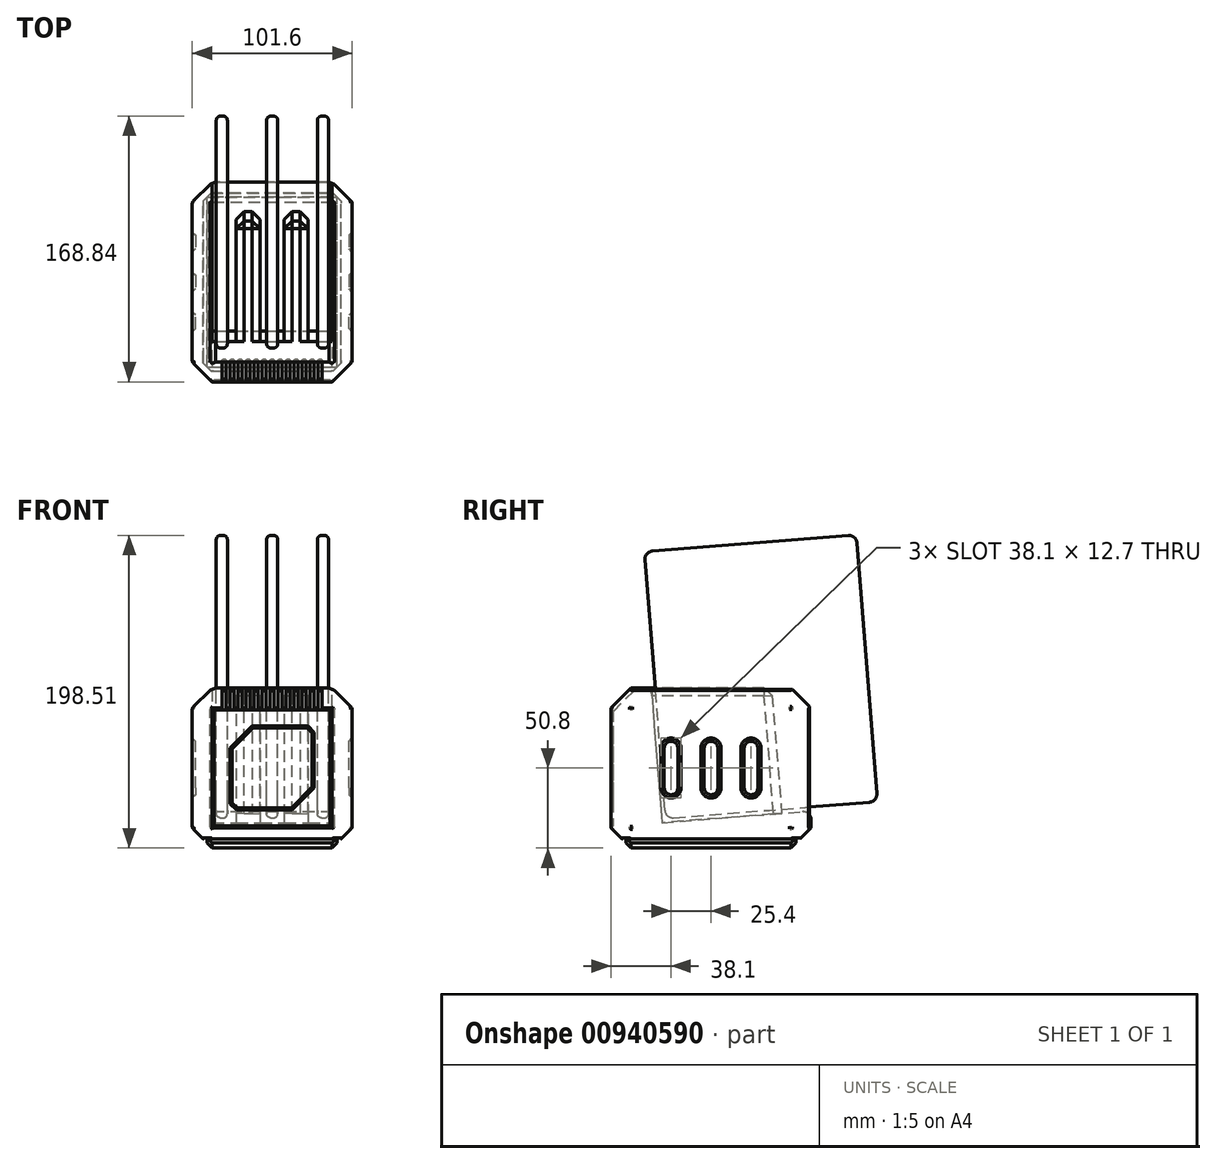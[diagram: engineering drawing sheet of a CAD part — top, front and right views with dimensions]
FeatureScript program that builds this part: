
annotation { "Feature Type Name" : "Feature", "Feature Type Description" : "" }
export const myFeature = defineFeature(function(context is Context, id is Id, definition is map)
    precondition{}
    {
        {
            var Q0;
            Q0=qCreatedBy(makeId("Front.planeOp"),FACE);
            var sketch = newSketch(context, id + "F0", { "sketchPlane" : qUnion([Q0])});
            skLineSegment(sketch, "E0.bottom", {"start": v(-50.8, 50.8) * mm, "end": v(50.8, 50.8) * mm});
            skLineSegment(sketch, "E0.top", {"start": v(-50.8, -50.8) * mm, "end": v(50.8, -50.8) * mm});
            skLineSegment(sketch, "E0.left", {"start": v(-50.8, 50.8) * mm, "end": v(-50.8, -50.8) * mm});
            skLineSegment(sketch, "E0.right", {"start": v(50.8, 50.8) * mm, "end": v(50.8, -50.8) * mm});
            skSolve(sketch);
        }
        {
            var Q0;
            Q0=makeQuery(id+"F0.imprint","IMPRINT",FACE,{"disambiguationData":[TD([[makeQuery(id+"F0.imprint","IMPRINT",EDGE,{"derivedFrom":sQuery(id+"F0.wireOp",EDGE,"E0.bottom")}),-1.0]])]});
            extrude(context, id + "F1", {"entities" : qUnion([Q0]), "endBound" : BoundingType.SYMMETRIC, "depth" : 127 * mm, "offsetDistance" : 25.4 * mm});
        }
        {
            var Q0;
            Q0=makeQuery(id+"F1.opExtrude","SWEPT_FACE",FACE,{"disambiguationData":[OSD([sQuery(id+"F0.wireOp",EDGE,"E0.bottom")])]});
            var Q1;
            Q1=makeQuery(id+"F1.opExtrude","SWEPT_FACE",FACE,{"disambiguationData":[OSD([sQuery(id+"F0.wireOp",EDGE,"E0.top")])]});
            var Q2;
            Q2=makeQuery(id+"F1.opExtrude","SWEPT_FACE",FACE,{"disambiguationData":[OSD([sQuery(id+"F0.wireOp",EDGE,"E0.right")])]});
            var Q3;
            Q3=makeQuery(id+"F1.opExtrude","CAP_FACE",FACE,{"disambiguationData":[OSD([sQuery(id+"F0.wireOp",EDGE,"E0.bottom"),sQuery(id+"F0.wireOp",EDGE,"E0.top"),sQuery(id+"F0.wireOp",EDGE,"E0.left"),sQuery(id+"F0.wireOp",EDGE,"E0.right")])],"isStart":false});
            var Q4;
            Q4=makeQuery(id+"F1.opExtrude","SWEPT_FACE",FACE,{"disambiguationData":[OSD([sQuery(id+"F0.wireOp",EDGE,"E0.left")])]});
            var Q5;
            Q5=makeQuery(id+"F1.opExtrude","CAP_FACE",FACE,{"disambiguationData":[OSD([sQuery(id+"F0.wireOp",EDGE,"E0.bottom"),sQuery(id+"F0.wireOp",EDGE,"E0.top"),sQuery(id+"F0.wireOp",EDGE,"E0.left"),sQuery(id+"F0.wireOp",EDGE,"E0.right")])],"isStart":true});
            chamfer(context, id + "F2", {"entities" : qUnion([Q0, Q1, Q2, Q3, Q4, Q5]), "width" : 12.7 * mm, "tangentPropagation" : true});
        }
        {
            var Q0;
            Q0=makeQuery(id+"F1.opExtrude","SWEPT_FACE",FACE,{"disambiguationData":[OSD([sQuery(id+"F0.wireOp",EDGE,"E0.left")])]});
            var sketch = newSketch(context, id + "F3", { "sketchPlane" : qUnion([Q0])});
            skArc(sketch, "E1", {"start": v(-19.05, 12.7) * mm, "mid": v(-25.4, 19.05) * mm, "end": v(-31.75, 12.7) * mm});
            skArc(sketch, "E2", {"start": v(6.35, 12.7) * mm, "mid": v(0, 19.05) * mm, "end": v(-6.35, 12.7) * mm});
            skLineSegment(sketch, "E3", {"start": v(-31.75, 12.7) * mm, "end": v(-31.75, -12.7) * mm});
            skArc(sketch, "E4.MirrorC", {"start": v(-19.05, -12.7) * mm, "mid": v(-25.4, -19.05) * mm, "end": v(-31.75, -12.7) * mm});
            skLineSegment(sketch, "E5", {"start": v(-19.05, 12.7) * mm, "end": v(-19.05, -12.7) * mm});
            skLineSegment(sketch, "E6.MirrorCS", {"start": v(31.75, 12.7) * mm, "end": v(31.75, -12.7) * mm});
            skLineSegment(sketch, "E7.MirrorCS", {"start": v(19.05, 12.7) * mm, "end": v(19.05, -12.7) * mm});
            skArc(sketch, "E8.MirrorCS", {"start": v(19.05, -12.7) * mm, "mid": v(25.4, -19.05) * mm, "end": v(31.75, -12.7) * mm});
            skArc(sketch, "E9.MirrorCS", {"start": v(19.05, 12.7) * mm, "mid": v(25.4, 19.05) * mm, "end": v(31.75, 12.7) * mm});
            skArc(sketch, "E10.MirrorC", {"start": v(6.35, -12.7) * mm, "mid": v(0, -19.05) * mm, "end": v(-6.35, -12.7) * mm});
            skLineSegment(sketch, "E11", {"start": v(-6.35, 12.7) * mm, "end": v(-6.35, -12.7) * mm});
            skLineSegment(sketch, "E12", {"start": v(6.35, 12.7) * mm, "end": v(6.35, -12.7) * mm});
            skSolve(sketch);
        }
        {
            var Q0;
            Q0 = qSketchRegion(id + "F3", true);
            extrude(context, id + "F4", {"entities" : qUnion([Q0]), "operationType" : NewBodyOperationType.REMOVE, "endBound" : BoundingType.UP_TO_NEXT, "oppositeDirection" : true, "depth" : 3.17 * mm, "offsetDistance" : 25.4 * mm});
        }
        {
            var Q0;
            Q0=qCreatedBy(makeId("Right.planeOp"),FACE);
            var sketch = newSketch(context, id + "F5", { "sketchPlane" : qUnion([Q0])});
            skLineSegment(sketch, "E13", {"start": v(-38, 51.03) * mm, "end": v(-31.18, -34.8) * mm});
            skLineSegment(sketch, "E14", {"start": v(-31.18, -34.8) * mm, "end": v(67.68, -26.97) * mm});
            skLineSegment(sketch, "E15", {"start": v(67.68, -26.97) * mm, "end": v(67.68, 51.44) * mm});
            skLineSegment(sketch, "E16", {"start": v(67.68, 51.44) * mm, "end": v(-38, 51.03) * mm});
            skSolve(sketch);
        }
        {
            var Q0;
            Q0=makeQuery(id+"F5.imprint","IMPRINT",FACE,{"disambiguationData":[TD([[makeQuery(id+"F5.imprint","IMPRINT",EDGE,{"derivedFrom":sQuery(id+"F5.wireOp",EDGE,"E13")}),1.0]])]});
            extrude(context, id + "F6", {"entities" : qUnion([Q0]), "operationType" : NewBodyOperationType.REMOVE, "endBound" : BoundingType.SYMMETRIC, "oppositeDirection" : true, "depth" : 76.2 * mm, "offsetDistance" : 25.4 * mm});
        }
        {
            var Q0;
            Q0=qCreatedBy(makeId("Front.planeOp"),FACE);
            var sketch = newSketch(context, id + "F7", { "sketchPlane" : qUnion([Q0])});
            skLineSegment(sketch, "E17.bottom", {"start": v(48.77, 38.1) * mm, "end": v(38.1, 38.1) * mm});
            skLineSegment(sketch, "E17.top", {"start": v(48.77, -38.1) * mm, "end": v(38.1, -38.1) * mm});
            skLineSegment(sketch, "E17.left", {"start": v(48.77, 38.1) * mm, "end": v(48.77, -38.1) * mm});
            skLineSegment(sketch, "E17.right", {"start": v(38.1, 38.1) * mm, "end": v(38.1, -38.1) * mm});
            skLineSegment(sketch, "E18.MirrorCS", {"start": v(-38.1, 38.1) * mm, "end": v(-38.1, -38.1) * mm});
            skLineSegment(sketch, "E19.MirrorCS", {"start": v(-48.77, -38.1) * mm, "end": v(-38.1, -38.1) * mm});
            skLineSegment(sketch, "E20.MirrorCS", {"start": v(-48.77, 38.1) * mm, "end": v(-38.1, 38.1) * mm});
            skLineSegment(sketch, "E21.MirrorCS", {"start": v(-48.77, 38.1) * mm, "end": v(-48.77, -38.1) * mm});
            skSolve(sketch);
        }
        {
            var Q0;
            Q0 = qSketchRegion(id + "F7", true);
            extrude(context, id + "F8", {"entities" : qUnion([Q0]), "operationType" : NewBodyOperationType.ADD, "endBound" : BoundingType.SYMMETRIC, "depth" : 101.6 * mm, "offsetDistance" : 25.4 * mm});
        }
        {
            var Q0;
            Q0=makeQuery(id+"F8.boolean.opBoolean","SPLIT",FACE,{"disambiguationData":[TD([makeQuery(id+"F4.boolean.opBoolean","COPY",FACE,{"derivedFrom":makeQuery(id+"F4.opExtrude","SWEPT_FACE",FACE,{"disambiguationData":[OSD([sQuery(id+"F3.wireOp",EDGE,"E1")])]})})])],"derivedFrom":makeQuery(id+"F8.opExtrude","SWEPT_FACE",FACE,{"disambiguationData":[OSD([sQuery(id+"F7.wireOp",EDGE,"E21.MirrorCS")])]})});
            var Q1;
            Q1=makeQuery(id+"F8.boolean.opBoolean","SPLIT",FACE,{"disambiguationData":[TD([makeQuery(id+"F4.boolean.opBoolean","COPY",FACE,{"derivedFrom":makeQuery(id+"F4.opExtrude","SWEPT_FACE",FACE,{"disambiguationData":[OSD([sQuery(id+"F3.wireOp",EDGE,"E2")])]})})])],"derivedFrom":makeQuery(id+"F8.opExtrude","SWEPT_FACE",FACE,{"disambiguationData":[OSD([sQuery(id+"F7.wireOp",EDGE,"E21.MirrorCS")])]})});
            var Q2;
            Q2=makeQuery(id+"F8.boolean.opBoolean","SPLIT",FACE,{"disambiguationData":[TD([makeQuery(id+"F4.boolean.opBoolean","COPY",FACE,{"derivedFrom":makeQuery(id+"F4.opExtrude","SWEPT_FACE",FACE,{"disambiguationData":[OSD([sQuery(id+"F3.wireOp",EDGE,"E6.MirrorCS")])]})})])],"derivedFrom":makeQuery(id+"F8.opExtrude","SWEPT_FACE",FACE,{"disambiguationData":[OSD([sQuery(id+"F7.wireOp",EDGE,"E21.MirrorCS")])]})});
            var Q3;
            Q3=makeQuery(id+"F8.boolean.opBoolean","SPLIT",FACE,{"disambiguationData":[TD([makeQuery(id+"F4.boolean.opBoolean","COPY",FACE,{"derivedFrom":makeQuery(id+"F4.opExtrude","SWEPT_FACE",FACE,{"disambiguationData":[OSD([sQuery(id+"F3.wireOp",EDGE,"E6.MirrorCS")])]})})])],"derivedFrom":makeQuery(id+"F8.opExtrude","SWEPT_FACE",FACE,{"disambiguationData":[OSD([sQuery(id+"F7.wireOp",EDGE,"E17.left")])]})});
            var Q4;
            Q4=makeQuery(id+"F8.boolean.opBoolean","SPLIT",FACE,{"disambiguationData":[TD([makeQuery(id+"F4.boolean.opBoolean","COPY",FACE,{"derivedFrom":makeQuery(id+"F4.opExtrude","SWEPT_FACE",FACE,{"disambiguationData":[OSD([sQuery(id+"F3.wireOp",EDGE,"E2")])]})})])],"derivedFrom":makeQuery(id+"F8.opExtrude","SWEPT_FACE",FACE,{"disambiguationData":[OSD([sQuery(id+"F7.wireOp",EDGE,"E17.left")])]})});
            var Q5;
            Q5=makeQuery(id+"F8.boolean.opBoolean","SPLIT",FACE,{"disambiguationData":[TD([makeQuery(id+"F4.boolean.opBoolean","COPY",FACE,{"derivedFrom":makeQuery(id+"F4.opExtrude","SWEPT_FACE",FACE,{"disambiguationData":[OSD([sQuery(id+"F3.wireOp",EDGE,"E1")])]})})])],"derivedFrom":makeQuery(id+"F8.opExtrude","SWEPT_FACE",FACE,{"disambiguationData":[OSD([sQuery(id+"F7.wireOp",EDGE,"E17.left")])]})});
            chamfer(context, id + "F9", {"entities" : qUnion([Q0, Q1, Q2, Q3, Q4, Q5]), "width" : 2.03 * mm, "tangentPropagation" : true});
        }
        {
            var Q0;
            Q0=makeQuery(id+"F1.opExtrude","SWEPT_FACE",FACE,{"disambiguationData":[OSD([sQuery(id+"F0.wireOp",EDGE,"E0.top")])]});
            var sketch = newSketch(context, id + "F10", { "sketchPlane" : qUnion([Q0])});
            skLineSegment(sketch, "E22.bottom", {"start": v(-41.28, 53.97) * mm, "end": v(41.27, 53.98) * mm});
            skLineSegment(sketch, "E22.top", {"start": v(-41.27, -53.98) * mm, "end": v(41.27, -53.97) * mm});
            skLineSegment(sketch, "E22.left", {"start": v(-41.28, 53.97) * mm, "end": v(-41.28, -53.98) * mm});
            skLineSegment(sketch, "E22.right", {"start": v(41.27, 53.98) * mm, "end": v(41.27, -53.97) * mm});
            skLineSegment(sketch, "E23.bottom", {"start": v(-43.82, 56.51) * mm, "end": v(43.81, 56.52) * mm});
            skLineSegment(sketch, "E23.top", {"start": v(-43.81, -56.52) * mm, "end": v(43.81, -56.51) * mm});
            skLineSegment(sketch, "E23.left", {"start": v(-43.82, 56.51) * mm, "end": v(-43.82, -56.52) * mm});
            skLineSegment(sketch, "E23.right", {"start": v(43.81, 56.52) * mm, "end": v(43.81, -56.51) * mm});
            skSolve(sketch);
        }
        {
            var Q0;
            Q0 = qSketchRegion(id + "F10", true);
            extrude(context, id + "F11", {"entities" : qUnion([Q0]), "operationType" : NewBodyOperationType.REMOVE, "oppositeDirection" : true, "depth" : 6.35 * mm, "offsetDistance" : 25.4 * mm});
        }
        {
            var Q0;
            {var subQ0=sQuery(id+"F0.wireOp",EDGE,"E0.right");var subQ1=sQuery(id+"F0.wireOp",EDGE,"E0.bottom");var subQ2=makeQuery(id+"F1.opExtrude","SWEPT_EDGE",EDGE,{"disambiguationData":[OSD([subQ1,subQ0])]});Q0=makeQuery(id+"F6.boolean.opBoolean","SPLIT",EDGE,{"disambiguationData":[topologyDisambiguationEdgeConnected([makeQuery(id+"F6.opExtrude","CAP_FACE",FACE,{"disambiguationData":[OSD([sQuery(id+"F5.wireOp",EDGE,"E13"),sQuery(id+"F5.wireOp",EDGE,"E14"),sQuery(id+"F5.wireOp",EDGE,"E15"),sQuery(id+"F5.wireOp",EDGE,"E16")])],"isStart":true})])],"derivedFrom":makeQuery(id+"F2.opChamfer","BLEND_EDGE",EDGE,{"blendedFrom":[subQ2,makeQuery(id+"F1.opExtrude","SWEPT_FACE",FACE,{"disambiguationData":[OSD([subQ1])]})],"blendedInto":[makeQuery(id+"F1.opExtrude","SWEPT_FACE",FACE,{"disambiguationData":[OSD([subQ1])]})]})});}
            var Q1;
            {var subQ0=sQuery(id+"F0.wireOp",EDGE,"E0.left");var subQ1=sQuery(id+"F0.wireOp",EDGE,"E0.bottom");var subQ2=makeQuery(id+"F1.opExtrude","SWEPT_EDGE",EDGE,{"disambiguationData":[OSD([subQ1,subQ0])]});Q1=makeQuery(id+"F6.boolean.opBoolean","SPLIT",EDGE,{"disambiguationData":[topologyDisambiguationEdgeConnected([makeQuery(id+"F6.opExtrude","CAP_FACE",FACE,{"disambiguationData":[OSD([sQuery(id+"F5.wireOp",EDGE,"E13"),sQuery(id+"F5.wireOp",EDGE,"E14"),sQuery(id+"F5.wireOp",EDGE,"E15"),sQuery(id+"F5.wireOp",EDGE,"E16")])],"isStart":false})])],"derivedFrom":makeQuery(id+"F2.opChamfer","BLEND_EDGE",EDGE,{"blendedFrom":[subQ2,makeQuery(id+"F1.opExtrude","SWEPT_FACE",FACE,{"disambiguationData":[OSD([subQ1])]})],"blendedInto":[makeQuery(id+"F1.opExtrude","SWEPT_FACE",FACE,{"disambiguationData":[OSD([subQ1])]})]})});}
            var Q2;
            {var subQ0=sQuery(id+"F0.wireOp",EDGE,"E0.right");var subQ1=makeQuery(id+"F1.opExtrude","CAP_EDGE",EDGE,{"disambiguationData":[OSD([subQ0])],"isStart":true});Q2=makeQuery(id+"F6.boolean.opBoolean","SPLIT",EDGE,{"disambiguationData":[topologyDisambiguationEdgeConnected([makeQuery(id+"F6.opExtrude","CAP_FACE",FACE,{"disambiguationData":[OSD([sQuery(id+"F5.wireOp",EDGE,"E13"),sQuery(id+"F5.wireOp",EDGE,"E14"),sQuery(id+"F5.wireOp",EDGE,"E15"),sQuery(id+"F5.wireOp",EDGE,"E16")])],"isStart":true})])],"derivedFrom":makeQuery(id+"F2.opChamfer","BLEND_EDGE",EDGE,{"blendedFrom":[subQ1,makeQuery(id+"F1.opExtrude","CAP_FACE",FACE,{"disambiguationData":[OSD([sQuery(id+"F0.wireOp",EDGE,"E0.bottom"),sQuery(id+"F0.wireOp",EDGE,"E0.top"),sQuery(id+"F0.wireOp",EDGE,"E0.left"),subQ0])],"isStart":true})],"blendedInto":[makeQuery(id+"F1.opExtrude","CAP_FACE",FACE,{"disambiguationData":[OSD([sQuery(id+"F0.wireOp",EDGE,"E0.bottom"),sQuery(id+"F0.wireOp",EDGE,"E0.top"),sQuery(id+"F0.wireOp",EDGE,"E0.left"),subQ0])],"isStart":true})]})});}
            var Q3;
            {var subQ0=sQuery(id+"F0.wireOp",EDGE,"E0.left");var subQ1=makeQuery(id+"F1.opExtrude","CAP_EDGE",EDGE,{"disambiguationData":[OSD([subQ0])],"isStart":true});Q3=makeQuery(id+"F6.boolean.opBoolean","SPLIT",EDGE,{"disambiguationData":[topologyDisambiguationEdgeConnected([makeQuery(id+"F6.opExtrude","CAP_FACE",FACE,{"disambiguationData":[OSD([sQuery(id+"F5.wireOp",EDGE,"E13"),sQuery(id+"F5.wireOp",EDGE,"E14"),sQuery(id+"F5.wireOp",EDGE,"E15"),sQuery(id+"F5.wireOp",EDGE,"E16")])],"isStart":false})])],"derivedFrom":makeQuery(id+"F2.opChamfer","BLEND_EDGE",EDGE,{"blendedFrom":[subQ1,makeQuery(id+"F1.opExtrude","CAP_FACE",FACE,{"disambiguationData":[OSD([sQuery(id+"F0.wireOp",EDGE,"E0.bottom"),sQuery(id+"F0.wireOp",EDGE,"E0.top"),subQ0,sQuery(id+"F0.wireOp",EDGE,"E0.right")])],"isStart":true})],"blendedInto":[makeQuery(id+"F1.opExtrude","CAP_FACE",FACE,{"disambiguationData":[OSD([sQuery(id+"F0.wireOp",EDGE,"E0.bottom"),sQuery(id+"F0.wireOp",EDGE,"E0.top"),subQ0,sQuery(id+"F0.wireOp",EDGE,"E0.right")])],"isStart":true})]})});}
            var Q4;
            {var subQ0=sQuery(id+"F0.wireOp",EDGE,"E0.bottom");Q4=makeQuery(id+"F2.opChamfer","BLEND_EDGE",EDGE,{"blendedFrom":[makeQuery(id+"F1.opExtrude","CAP_VERTEX",VERTEX,{"disambiguationData":[OSD([subQ0,sQuery(id+"F0.wireOp",EDGE,"E0.right")])],"isStart":true}),makeQuery(id+"F1.opExtrude","CAP_EDGE",EDGE,{"disambiguationData":[OSD([subQ0])],"isStart":true})],"blendedInto":[]});}
            var Q5;
            {var subQ0=sQuery(id+"F0.wireOp",EDGE,"E0.bottom");Q5=makeQuery(id+"F2.opChamfer","BLEND_EDGE",EDGE,{"blendedFrom":[makeQuery(id+"F1.opExtrude","CAP_VERTEX",VERTEX,{"disambiguationData":[OSD([subQ0,sQuery(id+"F0.wireOp",EDGE,"E0.left")])],"isStart":true}),makeQuery(id+"F1.opExtrude","CAP_EDGE",EDGE,{"disambiguationData":[OSD([subQ0])],"isStart":true})],"blendedInto":[]});}
            chamfer(context, id + "F12", {"entities" : qUnion([Q0, Q1, Q2, Q3, Q4, Q5]), "width" : 5.08 * mm, "tangentPropagation" : true});
        }
        {
            var Q0;
            Q0=makeQuery(id+"F1.opExtrude","CAP_FACE",FACE,{"disambiguationData":[OSD([sQuery(id+"F0.wireOp",EDGE,"E0.bottom"),sQuery(id+"F0.wireOp",EDGE,"E0.top"),sQuery(id+"F0.wireOp",EDGE,"E0.left"),sQuery(id+"F0.wireOp",EDGE,"E0.right")])],"isStart":false});
            var sketch = newSketch(context, id + "F13", { "sketchPlane" : qUnion([Q0])});
            skLineSegment(sketch, "E24.bottom", {"start": v(-12.16, 25.4) * mm, "end": v(22.13, 25.4) * mm});
            skLineSegment(sketch, "E24.top", {"start": v(-22.13, -25.4) * mm, "end": v(12.16, -25.4) * mm});
            skLineSegment(sketch, "E24.left", {"start": v(-25.4, 12.16) * mm, "end": v(-25.4, -22.13) * mm});
            skLineSegment(sketch, "E24.right", {"start": v(25.4, 22.13) * mm, "end": v(25.4, -12.16) * mm});
            skLineSegment(sketch, "E25", {"start": v(-12.16, 25.4) * mm, "end": v(-25.4, 12.16) * mm});
            skLineSegment(sketch, "E26", {"start": v(22.13, 25.4) * mm, "end": v(25.4, 22.13) * mm});
            skLineSegment(sketch, "E27", {"start": v(-25.4, -22.13) * mm, "end": v(-22.13, -25.4) * mm});
            skLineSegment(sketch, "E28", {"start": v(25.4, -12.16) * mm, "end": v(12.16, -25.4) * mm});
            skSolve(sketch);
        }
        {
            var Q0;
            Q0=makeQuery(id+"F13.imprint","IMPRINT",FACE,{"disambiguationData":[TD([[makeQuery(id+"F13.imprint","IMPRINT",EDGE,{"derivedFrom":sQuery(id+"F13.wireOp",EDGE,"E24.bottom")}),1.0]])]});
            extrude(context, id + "F14", {"entities" : qUnion([Q0]), "operationType" : NewBodyOperationType.REMOVE, "oppositeDirection" : true, "depth" : 1.27 * mm, "offsetDistance" : 25.4 * mm});
        }
        {
            var Q0;
            Q0=makeQuery(id+"F14.boolean.opBoolean","COPY",FACE,{"derivedFrom":makeQuery(id+"F14.opExtrude","CAP_FACE",FACE,{"disambiguationData":[OSD([sQuery(id+"F0.wireOp",EDGE,"E0.bottom"),sQuery(id+"F0.wireOp",EDGE,"E0.top"),sQuery(id+"F0.wireOp",EDGE,"E0.left"),sQuery(id+"F0.wireOp",EDGE,"E0.right"),sQuery(id+"F13.wireOp",EDGE,"E24.bottom"),sQuery(id+"F13.wireOp",EDGE,"E24.top"),sQuery(id+"F13.wireOp",EDGE,"E24.left"),sQuery(id+"F13.wireOp",EDGE,"E24.right"),sQuery(id+"F13.wireOp",EDGE,"E25"),sQuery(id+"F13.wireOp",EDGE,"E26"),sQuery(id+"F13.wireOp",EDGE,"E27"),sQuery(id+"F13.wireOp",EDGE,"E28")])],"isStart":false})});
            chamfer(context, id + "F15", {"entities" : qUnion([Q0]), "width" : 1.27 * mm, "tangentPropagation" : true});
        }
        {
            var Q0;
            Q0=makeQuery(id+"F6.boolean.opBoolean","COPY",FACE,{"derivedFrom":makeQuery(id+"F6.opExtrude","SWEPT_FACE",FACE,{"disambiguationData":[OSD([sQuery(id+"F5.wireOp",EDGE,"E13")])]})});
            var sketch = newSketch(context, id + "F16", { "sketchPlane" : qUnion([Q0])});
            skLineSegment(sketch, "E29.bottom", {"start": v(-22.86, 53.65) * mm, "end": v(-7.62, 53.65) * mm});
            skLineSegment(sketch, "E29.top", {"start": v(-22.86, -32.21) * mm, "end": v(-7.62, -32.21) * mm});
            skLineSegment(sketch, "E29.left", {"start": v(-22.86, 53.65) * mm, "end": v(-22.86, -32.21) * mm});
            skLineSegment(sketch, "E29.right", {"start": v(-7.62, 53.65) * mm, "end": v(-7.62, -32.21) * mm});
            skLineSegment(sketch, "E30.bottom", {"start": v(7.62, 53.65) * mm, "end": v(22.86, 53.65) * mm});
            skLineSegment(sketch, "E30.top", {"start": v(7.62, -32.21) * mm, "end": v(22.86, -32.21) * mm});
            skLineSegment(sketch, "E30.left", {"start": v(7.62, 53.65) * mm, "end": v(7.62, -32.21) * mm});
            skLineSegment(sketch, "E30.right", {"start": v(22.86, 53.65) * mm, "end": v(22.86, -32.21) * mm});
            skSolve(sketch);
        }
        {
            var Q0;
            Q0 = qSketchRegion(id + "F16", true);
            extrude(context, id + "F17", {"entities" : qUnion([Q0]), "operationType" : NewBodyOperationType.ADD, "depth" : 76.2 * mm, "offsetDistance" : 25.4 * mm});
        }
        {
            var Q0;
            Q0=qCreatedBy(makeId("Right.planeOp"),FACE);
            var sketch = newSketch(context, id + "F18", { "sketchPlane" : qUnion([Q0])});
            skLineSegment(sketch, "E31.bottom", {"start": v(-40.6, 58.82) * mm, "end": v(48.43, 58.82) * mm});
            skLineSegment(sketch, "E31.top", {"start": v(-40.6, 50.8) * mm, "end": v(48.43, 50.8) * mm});
            skLineSegment(sketch, "E31.left", {"start": v(-40.6, 58.82) * mm, "end": v(-40.6, 50.8) * mm});
            skLineSegment(sketch, "E31.right", {"start": v(48.43, 58.82) * mm, "end": v(48.43, 50.8) * mm});
            skSolve(sketch);
        }
        {
            var Q0;
            Q0=makeQuery(id+"F18.imprint","IMPRINT",FACE,{"disambiguationData":[TD([[makeQuery(id+"F18.imprint","IMPRINT",EDGE,{"derivedFrom":sQuery(id+"F18.wireOp",EDGE,"E31.bottom")}),-1.0]])]});
            extrude(context, id + "F19", {"entities" : qUnion([Q0]), "operationType" : NewBodyOperationType.REMOVE, "endBound" : BoundingType.SYMMETRIC, "oppositeDirection" : true, "depth" : 101.6 * mm, "offsetDistance" : 25.4 * mm});
        }
        {
            var Q0;
            Q0=makeQuery(id+"F19.boolean.opBoolean","INTERSECT",EDGE,{"derivedFrom":[makeQuery(id+"F17.opExtrude","SWEPT_FACE",FACE,{"disambiguationData":[OSD([sQuery(id+"F16.wireOp",EDGE,"E29.left")])]}),makeQuery(id+"F19.opExtrude","SWEPT_FACE",FACE,{"disambiguationData":[OSD([sQuery(id+"F18.wireOp",EDGE,"E31.top")])]})]});
            var Q1;
            Q1=makeQuery(id+"F19.boolean.opBoolean","INTERSECT",EDGE,{"derivedFrom":[makeQuery(id+"F17.opExtrude","SWEPT_FACE",FACE,{"disambiguationData":[OSD([sQuery(id+"F16.wireOp",EDGE,"E29.right")])]}),makeQuery(id+"F19.opExtrude","SWEPT_FACE",FACE,{"disambiguationData":[OSD([sQuery(id+"F18.wireOp",EDGE,"E31.top")])]})]});
            var Q2;
            Q2=makeQuery(id+"F19.boolean.opBoolean","INTERSECT",EDGE,{"derivedFrom":[makeQuery(id+"F17.opExtrude","SWEPT_FACE",FACE,{"disambiguationData":[OSD([sQuery(id+"F16.wireOp",EDGE,"E30.left")])]}),makeQuery(id+"F19.opExtrude","SWEPT_FACE",FACE,{"disambiguationData":[OSD([sQuery(id+"F18.wireOp",EDGE,"E31.top")])]})]});
            var Q3;
            Q3=makeQuery(id+"F19.boolean.opBoolean","INTERSECT",EDGE,{"derivedFrom":[makeQuery(id+"F17.opExtrude","SWEPT_FACE",FACE,{"disambiguationData":[OSD([sQuery(id+"F16.wireOp",EDGE,"E30.right")])]}),makeQuery(id+"F19.opExtrude","SWEPT_FACE",FACE,{"disambiguationData":[OSD([sQuery(id+"F18.wireOp",EDGE,"E31.top")])]})]});
            var Q4;
            Q4=makeQuery(id+"F17.opExtrude","CAP_EDGE",EDGE,{"disambiguationData":[OSD([sQuery(id+"F16.wireOp",EDGE,"E29.right")])],"isStart":false});
            var Q5;
            Q5=makeQuery(id+"F17.opExtrude","CAP_EDGE",EDGE,{"disambiguationData":[OSD([sQuery(id+"F16.wireOp",EDGE,"E29.left")])],"isStart":false});
            var Q6;
            Q6=makeQuery(id+"F19.boolean.opBoolean","INTERSECT",EDGE,{"derivedFrom":[makeQuery(id+"F17.opExtrude","CAP_FACE",FACE,{"disambiguationData":[OSD([sQuery(id+"F16.wireOp",EDGE,"E29.bottom"),sQuery(id+"F16.wireOp",EDGE,"E29.top"),sQuery(id+"F16.wireOp",EDGE,"E29.left"),sQuery(id+"F16.wireOp",EDGE,"E29.right")])],"isStart":false}),makeQuery(id+"F19.opExtrude","SWEPT_FACE",FACE,{"disambiguationData":[OSD([sQuery(id+"F18.wireOp",EDGE,"E31.top")])]})]});
            var Q7;
            Q7=makeQuery(id+"F19.boolean.opBoolean","INTERSECT",EDGE,{"derivedFrom":[makeQuery(id+"F17.opExtrude","CAP_FACE",FACE,{"disambiguationData":[OSD([sQuery(id+"F16.wireOp",EDGE,"E30.bottom"),sQuery(id+"F16.wireOp",EDGE,"E30.top"),sQuery(id+"F16.wireOp",EDGE,"E30.left"),sQuery(id+"F16.wireOp",EDGE,"E30.right")])],"isStart":false}),makeQuery(id+"F19.opExtrude","SWEPT_FACE",FACE,{"disambiguationData":[OSD([sQuery(id+"F18.wireOp",EDGE,"E31.top")])]})]});
            var Q8;
            Q8=makeQuery(id+"F17.opExtrude","CAP_EDGE",EDGE,{"disambiguationData":[OSD([sQuery(id+"F16.wireOp",EDGE,"E30.left")])],"isStart":false});
            var Q9;
            Q9=makeQuery(id+"F17.opExtrude","CAP_EDGE",EDGE,{"disambiguationData":[OSD([sQuery(id+"F16.wireOp",EDGE,"E30.right")])],"isStart":false});
            chamfer(context, id + "F20", {"entities" : qUnion([Q0, Q1, Q2, Q3, Q4, Q5, Q6, Q7, Q8, Q9]), "width" : 5.08 * mm, "tangentPropagation" : true});
        }
        {
            var Q0;
            Q0=qCreatedBy(makeId("Right.planeOp"),FACE);
            var sketch = newSketch(context, id + "F21", { "sketchPlane" : qUnion([Q0])});
            skLineSegment(sketch, "E32.0", {"start": v(39.71, -29.16) * mm, "end": v(-31.18, -34.8) * mm});
            skLineSegment(sketch, "E33.0", {"start": v(-37.58, 45.72) * mm, "end": v(-31.18, -34.8) * mm});
            skLineSegment(sketch, "E34", {"start": v(-28.85, -32.06) * mm, "end": v(105.73, -21.37) * mm});
            skLineSegment(sketch, "E35", {"start": v(-28.85, -32.06) * mm, "end": v(-42.31, 137.4) * mm});
            skLineSegment(sketch, "E36", {"start": v(-42.31, 137.4) * mm, "end": v(92.26, 148.1) * mm});
            skLineSegment(sketch, "E37", {"start": v(105.73, -21.37) * mm, "end": v(92.26, 148.1) * mm});
            skSolve(sketch);
        }
        {
            var Q0;
            Q0=makeQuery(id+"F21.imprint","IMPRINT",FACE,{"disambiguationData":[TD([[makeQuery(id+"F21.imprint","IMPRINT",EDGE,{"derivedFrom":sQuery(id+"F21.wireOp",EDGE,"E34")}),1.0]])]});
            extrude(context, id + "F22", {"entities" : qUnion([Q0]), "endBound" : BoundingType.SYMMETRIC, "depth" : 7 * mm, "offsetDistance" : 25.4 * mm});
        }
        {
            var Q0;
            Q0=makeQuery(id+"F22.opExtrude","SWEPT_EDGE",EDGE,{"disambiguationData":[OSD([sQuery(id+"F21.wireOp",EDGE,"E36"),sQuery(id+"F21.wireOp",EDGE,"E37")])]});
            var Q1;
            Q1=makeQuery(id+"F22.opExtrude","SWEPT_EDGE",EDGE,{"disambiguationData":[OSD([sQuery(id+"F21.wireOp",EDGE,"E35"),sQuery(id+"F21.wireOp",EDGE,"E36")])]});
            var Q2;
            Q2=makeQuery(id+"F22.opExtrude","SWEPT_EDGE",EDGE,{"disambiguationData":[OSD([sQuery(id+"F21.wireOp",EDGE,"E34"),sQuery(id+"F21.wireOp",EDGE,"E37")])]});
            var Q3;
            Q3=makeQuery(id+"F22.opExtrude","SWEPT_EDGE",EDGE,{"disambiguationData":[OSD([sQuery(id+"F21.wireOp",EDGE,"E34"),sQuery(id+"F21.wireOp",EDGE,"E35")])]});
            fillet(context, id + "F23", {"entities" : qUnion([Q0, Q1, Q2, Q3]), "radius" : 5.08 * mm, "tangentPropagation" : true, "allowEdgeOverflow" : false});
        }
        {
            var Q0;
            Q0=makeQuery(id+"F22.opExtrude","CAP_FACE",FACE,{"disambiguationData":[OSD([sQuery(id+"F21.wireOp",EDGE,"E34"),sQuery(id+"F21.wireOp",EDGE,"E35"),sQuery(id+"F21.wireOp",EDGE,"E36"),sQuery(id+"F21.wireOp",EDGE,"E37")])],"isStart":false});
            var Q1;
            Q1=makeQuery(id+"F22.opExtrude","CAP_FACE",FACE,{"disambiguationData":[OSD([sQuery(id+"F21.wireOp",EDGE,"E34"),sQuery(id+"F21.wireOp",EDGE,"E35"),sQuery(id+"F21.wireOp",EDGE,"E36"),sQuery(id+"F21.wireOp",EDGE,"E37")])],"isStart":true});
            fillet(context, id + "F24", {"entities" : qUnion([Q0, Q1]), "radius" : 2.54 * mm, "tangentPropagation" : true, "allowEdgeOverflow" : false});
        }
        {
            var Q0;
            Q0=makeQuery(id+"F22.opExtrude","SWEPT_BODY",BODY,{"disambiguationData":[OSD([sQuery(id+"F21.wireOp",EDGE,"E34"),sQuery(id+"F21.wireOp",EDGE,"E35"),sQuery(id+"F21.wireOp",EDGE,"E36"),sQuery(id+"F21.wireOp",EDGE,"E37")])]});
            transform(context, id + "F25", {"entities" : qUnion([Q0]), "transformType" : TransformType.TRANSLATION_3D, "dx" : 32.26 * mm, "dy" : 0 * mm, "dz" : 0 * mm, "makeCopy" : true});
        }
        {
            var Q0;
            Q0=makeQuery(id+"F22.opExtrude","SWEPT_BODY",BODY,{"disambiguationData":[OSD([sQuery(id+"F21.wireOp",EDGE,"E34"),sQuery(id+"F21.wireOp",EDGE,"E35"),sQuery(id+"F21.wireOp",EDGE,"E36"),sQuery(id+"F21.wireOp",EDGE,"E37")])]});
            transform(context, id + "F26", {"entities" : qUnion([Q0]), "transformType" : TransformType.TRANSLATION_3D, "dx" : -32 * mm, "dy" : 0 * mm, "dz" : 0 * mm, "makeCopy" : true});
        }
        {
            var Q0;
            Q0=makeQuery(id+"F6.boolean.opBoolean","INTERSECT",EDGE,{"derivedFrom":[makeQuery(id+"F1.opExtrude","CAP_FACE",FACE,{"disambiguationData":[OSD([sQuery(id+"F0.wireOp",EDGE,"E0.bottom"),sQuery(id+"F0.wireOp",EDGE,"E0.top"),sQuery(id+"F0.wireOp",EDGE,"E0.left"),sQuery(id+"F0.wireOp",EDGE,"E0.right")])],"isStart":true}),makeQuery(id+"F6.opExtrude","SWEPT_FACE",FACE,{"disambiguationData":[OSD([sQuery(id+"F5.wireOp",EDGE,"E14")])]})]});
            fillet(context, id + "F27", {"entities" : qUnion([Q0]), "radius" : 5.08 * mm, "tangentPropagation" : true, "allowEdgeOverflow" : false});
        }
        {
            var Q0;
            {var subQ0=sQuery(id+"F0.wireOp",EDGE,"E0.left");Q0=makeQuery(id+"F2.opChamfer","BLEND_EDGE",EDGE,{"blendedFrom":[makeQuery(id+"F1.opExtrude","SWEPT_EDGE",EDGE,{"disambiguationData":[OSD([sQuery(id+"F0.wireOp",EDGE,"E0.bottom"),subQ0])]}),makeQuery(id+"F1.opExtrude","SWEPT_FACE",FACE,{"disambiguationData":[OSD([subQ0])]})],"blendedInto":[makeQuery(id+"F1.opExtrude","SWEPT_FACE",FACE,{"disambiguationData":[OSD([subQ0])]})]});}
            var Q1;
            {var subQ0=sQuery(id+"F0.wireOp",EDGE,"E0.left");Q1=makeQuery(id+"F2.opChamfer","BLEND_EDGE",EDGE,{"blendedFrom":[makeQuery(id+"F1.opExtrude","CAP_EDGE",EDGE,{"disambiguationData":[OSD([subQ0])],"isStart":true}),makeQuery(id+"F1.opExtrude","SWEPT_FACE",FACE,{"disambiguationData":[OSD([subQ0])]})],"blendedInto":[makeQuery(id+"F1.opExtrude","SWEPT_FACE",FACE,{"disambiguationData":[OSD([subQ0])]})]});}
            var Q2;
            {var subQ0=sQuery(id+"F0.wireOp",EDGE,"E0.left");var subQ1=sQuery(id+"F0.wireOp",EDGE,"E0.bottom");Q2=makeQuery(id+"F2.opChamfer","BLEND_EDGE",EDGE,{"blendedFrom":[makeQuery(id+"F1.opExtrude","CAP_VERTEX",VERTEX,{"disambiguationData":[OSD([subQ1,subQ0])],"isStart":true}),makeQuery(id+"F1.opExtrude","SWEPT_EDGE",EDGE,{"disambiguationData":[OSD([subQ1,subQ0])]})],"blendedInto":[]});}
            var Q3;
            {var subQ0=sQuery(id+"F0.wireOp",EDGE,"E0.left");Q3=makeQuery(id+"F2.opChamfer","BLEND_EDGE",EDGE,{"blendedFrom":[makeQuery(id+"F1.opExtrude","CAP_VERTEX",VERTEX,{"disambiguationData":[OSD([sQuery(id+"F0.wireOp",EDGE,"E0.bottom"),subQ0])],"isStart":true}),makeQuery(id+"F1.opExtrude","CAP_EDGE",EDGE,{"disambiguationData":[OSD([subQ0])],"isStart":true})],"blendedInto":[]});}
            var Q4;
            {var subQ0=sQuery(id+"F0.wireOp",EDGE,"E0.left");var subQ1=sQuery(id+"F0.wireOp",EDGE,"E0.bottom");Q4=makeQuery(id+"F2.opChamfer","BLEND_EDGE",EDGE,{"blendedFrom":[makeQuery(id+"F1.opExtrude","CAP_VERTEX",VERTEX,{"disambiguationData":[OSD([subQ1,subQ0])],"isStart":false}),makeQuery(id+"F1.opExtrude","SWEPT_EDGE",EDGE,{"disambiguationData":[OSD([subQ1,subQ0])]})],"blendedInto":[]});}
            var Q5;
            {var subQ0=sQuery(id+"F0.wireOp",EDGE,"E0.left");Q5=makeQuery(id+"F2.opChamfer","BLEND_EDGE",EDGE,{"blendedFrom":[makeQuery(id+"F1.opExtrude","CAP_VERTEX",VERTEX,{"disambiguationData":[OSD([sQuery(id+"F0.wireOp",EDGE,"E0.bottom"),subQ0])],"isStart":false}),makeQuery(id+"F1.opExtrude","CAP_EDGE",EDGE,{"disambiguationData":[OSD([subQ0])],"isStart":false})],"blendedInto":[]});}
            var Q6;
            {var subQ0=sQuery(id+"F0.wireOp",EDGE,"E0.left");Q6=makeQuery(id+"F2.opChamfer","BLEND_EDGE",EDGE,{"blendedFrom":[makeQuery(id+"F1.opExtrude","CAP_EDGE",EDGE,{"disambiguationData":[OSD([subQ0])],"isStart":false}),makeQuery(id+"F1.opExtrude","SWEPT_FACE",FACE,{"disambiguationData":[OSD([subQ0])]})],"blendedInto":[makeQuery(id+"F1.opExtrude","SWEPT_FACE",FACE,{"disambiguationData":[OSD([subQ0])]})]});}
            var Q7;
            {var subQ0=sQuery(id+"F0.wireOp",EDGE,"E0.bottom");Q7=makeQuery(id+"F2.opChamfer","BLEND_EDGE",EDGE,{"blendedFrom":[makeQuery(id+"F1.opExtrude","CAP_VERTEX",VERTEX,{"disambiguationData":[OSD([subQ0,sQuery(id+"F0.wireOp",EDGE,"E0.left")])],"isStart":false}),makeQuery(id+"F1.opExtrude","CAP_EDGE",EDGE,{"disambiguationData":[OSD([subQ0])],"isStart":false})],"blendedInto":[]});}
            var Q8;
            {var subQ0=sQuery(id+"F0.wireOp",EDGE,"E0.left");Q8=makeQuery(id+"F2.opChamfer","BLEND_EDGE",EDGE,{"blendedFrom":[makeQuery(id+"F1.opExtrude","SWEPT_EDGE",EDGE,{"disambiguationData":[OSD([sQuery(id+"F0.wireOp",EDGE,"E0.top"),subQ0])]}),makeQuery(id+"F1.opExtrude","SWEPT_FACE",FACE,{"disambiguationData":[OSD([subQ0])]})],"blendedInto":[makeQuery(id+"F1.opExtrude","SWEPT_FACE",FACE,{"disambiguationData":[OSD([subQ0])]})]});}
            var Q9;
            {var subQ0=sQuery(id+"F0.wireOp",EDGE,"E0.left");Q9=makeQuery(id+"F2.opChamfer","BLEND_EDGE",EDGE,{"blendedFrom":[makeQuery(id+"F1.opExtrude","CAP_VERTEX",VERTEX,{"disambiguationData":[OSD([sQuery(id+"F0.wireOp",EDGE,"E0.top"),subQ0])],"isStart":false}),makeQuery(id+"F1.opExtrude","CAP_EDGE",EDGE,{"disambiguationData":[OSD([subQ0])],"isStart":false})],"blendedInto":[]});}
            var Q10;
            {var subQ0=sQuery(id+"F0.wireOp",EDGE,"E0.left");var subQ1=sQuery(id+"F0.wireOp",EDGE,"E0.top");var subQ2=makeQuery(id+"F1.opExtrude","SWEPT_EDGE",EDGE,{"disambiguationData":[OSD([subQ1,subQ0])]});var subQ3=makeQuery(id+"F1.opExtrude","CAP_VERTEX",VERTEX,{"disambiguationData":[OSD([subQ1,subQ0])],"isStart":false});Q10=makeQuery(id+"F11.boolean.opBoolean","SPLIT",EDGE,{"disambiguationData":[TD([makeQuery(id+"F1.opExtrude","SWEPT_FACE",FACE,{"disambiguationData":[OSD([subQ0])]})])],"derivedFrom":makeQuery(id+"F2.opChamfer","BLEND_EDGE",EDGE,{"blendedFrom":[subQ3,subQ2],"blendedInto":[]})});}
            var Q11;
            {var subQ0=sQuery(id+"F0.wireOp",EDGE,"E0.left");var subQ1=sQuery(id+"F0.wireOp",EDGE,"E0.top");var subQ2=makeQuery(id+"F1.opExtrude","CAP_EDGE",EDGE,{"disambiguationData":[OSD([subQ1])],"isStart":false});var subQ3=makeQuery(id+"F1.opExtrude","CAP_VERTEX",VERTEX,{"disambiguationData":[OSD([subQ1,subQ0])],"isStart":false});Q11=makeQuery(id+"F11.boolean.opBoolean","SPLIT",EDGE,{"disambiguationData":[TD([makeQuery(id+"F11.opExtrude","SWEPT_FACE",FACE,{"disambiguationData":[OSD([sQuery(id+"F10.wireOp",EDGE,"E23.bottom")])]})])],"derivedFrom":makeQuery(id+"F2.opChamfer","BLEND_EDGE",EDGE,{"blendedFrom":[subQ3,subQ2],"blendedInto":[]})});}
            var Q12;
            {var subQ0=sQuery(id+"F0.wireOp",EDGE,"E0.bottom");Q12=makeQuery(id+"F2.opChamfer","BLEND_EDGE",EDGE,{"blendedFrom":[makeQuery(id+"F1.opExtrude","CAP_VERTEX",VERTEX,{"disambiguationData":[OSD([subQ0,sQuery(id+"F0.wireOp",EDGE,"E0.right")])],"isStart":false}),makeQuery(id+"F1.opExtrude","CAP_EDGE",EDGE,{"disambiguationData":[OSD([subQ0])],"isStart":false})],"blendedInto":[]});}
            var Q13;
            {var subQ0=sQuery(id+"F0.wireOp",EDGE,"E0.right");var subQ1=sQuery(id+"F0.wireOp",EDGE,"E0.bottom");Q13=makeQuery(id+"F2.opChamfer","BLEND_EDGE",EDGE,{"blendedFrom":[makeQuery(id+"F1.opExtrude","CAP_VERTEX",VERTEX,{"disambiguationData":[OSD([subQ1,subQ0])],"isStart":false}),makeQuery(id+"F1.opExtrude","SWEPT_EDGE",EDGE,{"disambiguationData":[OSD([subQ1,subQ0])]})],"blendedInto":[]});}
            var Q14;
            {var subQ0=sQuery(id+"F0.wireOp",EDGE,"E0.right");Q14=makeQuery(id+"F2.opChamfer","BLEND_EDGE",EDGE,{"blendedFrom":[makeQuery(id+"F1.opExtrude","CAP_VERTEX",VERTEX,{"disambiguationData":[OSD([sQuery(id+"F0.wireOp",EDGE,"E0.bottom"),subQ0])],"isStart":false}),makeQuery(id+"F1.opExtrude","CAP_EDGE",EDGE,{"disambiguationData":[OSD([subQ0])],"isStart":false})],"blendedInto":[]});}
            var Q15;
            {var subQ0=sQuery(id+"F0.wireOp",EDGE,"E0.right");Q15=makeQuery(id+"F2.opChamfer","BLEND_EDGE",EDGE,{"blendedFrom":[makeQuery(id+"F1.opExtrude","CAP_EDGE",EDGE,{"disambiguationData":[OSD([subQ0])],"isStart":false}),makeQuery(id+"F1.opExtrude","SWEPT_FACE",FACE,{"disambiguationData":[OSD([subQ0])]})],"blendedInto":[makeQuery(id+"F1.opExtrude","SWEPT_FACE",FACE,{"disambiguationData":[OSD([subQ0])]})]});}
            var Q16;
            {var subQ0=sQuery(id+"F0.wireOp",EDGE,"E0.right");Q16=makeQuery(id+"F2.opChamfer","BLEND_EDGE",EDGE,{"blendedFrom":[makeQuery(id+"F1.opExtrude","SWEPT_EDGE",EDGE,{"disambiguationData":[OSD([sQuery(id+"F0.wireOp",EDGE,"E0.bottom"),subQ0])]}),makeQuery(id+"F1.opExtrude","SWEPT_FACE",FACE,{"disambiguationData":[OSD([subQ0])]})],"blendedInto":[makeQuery(id+"F1.opExtrude","SWEPT_FACE",FACE,{"disambiguationData":[OSD([subQ0])]})]});}
            var Q17;
            {var subQ0=sQuery(id+"F0.wireOp",EDGE,"E0.right");var subQ1=sQuery(id+"F0.wireOp",EDGE,"E0.bottom");Q17=makeQuery(id+"F2.opChamfer","BLEND_EDGE",EDGE,{"blendedFrom":[makeQuery(id+"F1.opExtrude","CAP_VERTEX",VERTEX,{"disambiguationData":[OSD([subQ1,subQ0])],"isStart":true}),makeQuery(id+"F1.opExtrude","SWEPT_EDGE",EDGE,{"disambiguationData":[OSD([subQ1,subQ0])]})],"blendedInto":[]});}
            var Q18;
            {var subQ0=sQuery(id+"F0.wireOp",EDGE,"E0.right");Q18=makeQuery(id+"F2.opChamfer","BLEND_EDGE",EDGE,{"blendedFrom":[makeQuery(id+"F1.opExtrude","CAP_VERTEX",VERTEX,{"disambiguationData":[OSD([sQuery(id+"F0.wireOp",EDGE,"E0.bottom"),subQ0])],"isStart":true}),makeQuery(id+"F1.opExtrude","CAP_EDGE",EDGE,{"disambiguationData":[OSD([subQ0])],"isStart":true})],"blendedInto":[]});}
            var Q19;
            {var subQ0=sQuery(id+"F0.wireOp",EDGE,"E0.right");Q19=makeQuery(id+"F2.opChamfer","BLEND_EDGE",EDGE,{"blendedFrom":[makeQuery(id+"F1.opExtrude","CAP_EDGE",EDGE,{"disambiguationData":[OSD([subQ0])],"isStart":true}),makeQuery(id+"F1.opExtrude","SWEPT_FACE",FACE,{"disambiguationData":[OSD([subQ0])]})],"blendedInto":[makeQuery(id+"F1.opExtrude","SWEPT_FACE",FACE,{"disambiguationData":[OSD([subQ0])]})]});}
            var Q20;
            {var subQ0=sQuery(id+"F0.wireOp",EDGE,"E0.right");Q20=makeQuery(id+"F2.opChamfer","BLEND_EDGE",EDGE,{"blendedFrom":[makeQuery(id+"F1.opExtrude","SWEPT_EDGE",EDGE,{"disambiguationData":[OSD([sQuery(id+"F0.wireOp",EDGE,"E0.top"),subQ0])]}),makeQuery(id+"F1.opExtrude","SWEPT_FACE",FACE,{"disambiguationData":[OSD([subQ0])]})],"blendedInto":[makeQuery(id+"F1.opExtrude","SWEPT_FACE",FACE,{"disambiguationData":[OSD([subQ0])]})]});}
            var Q21;
            {var subQ0=sQuery(id+"F0.wireOp",EDGE,"E0.right");var subQ1=sQuery(id+"F0.wireOp",EDGE,"E0.top");var subQ2=makeQuery(id+"F1.opExtrude","SWEPT_EDGE",EDGE,{"disambiguationData":[OSD([subQ1,subQ0])]});var subQ3=makeQuery(id+"F1.opExtrude","CAP_VERTEX",VERTEX,{"disambiguationData":[OSD([subQ1,subQ0])],"isStart":false});Q21=makeQuery(id+"F11.boolean.opBoolean","SPLIT",EDGE,{"disambiguationData":[TD([makeQuery(id+"F1.opExtrude","SWEPT_FACE",FACE,{"disambiguationData":[OSD([subQ0])]})])],"derivedFrom":makeQuery(id+"F2.opChamfer","BLEND_EDGE",EDGE,{"blendedFrom":[subQ3,subQ2],"blendedInto":[]})});}
            var Q22;
            {var subQ0=sQuery(id+"F0.wireOp",EDGE,"E0.right");var subQ1=sQuery(id+"F0.wireOp",EDGE,"E0.top");var subQ2=makeQuery(id+"F1.opExtrude","SWEPT_EDGE",EDGE,{"disambiguationData":[OSD([subQ1,subQ0])]});var subQ3=makeQuery(id+"F1.opExtrude","CAP_VERTEX",VERTEX,{"disambiguationData":[OSD([subQ1,subQ0])],"isStart":true});Q22=makeQuery(id+"F11.boolean.opBoolean","SPLIT",EDGE,{"disambiguationData":[TD([makeQuery(id+"F1.opExtrude","SWEPT_FACE",FACE,{"disambiguationData":[OSD([subQ0])]})])],"derivedFrom":makeQuery(id+"F2.opChamfer","BLEND_EDGE",EDGE,{"blendedFrom":[subQ3,subQ2],"blendedInto":[]})});}
            var Q23;
            {var subQ0=sQuery(id+"F0.wireOp",EDGE,"E0.right");var subQ1=sQuery(id+"F0.wireOp",EDGE,"E0.top");var subQ2=makeQuery(id+"F1.opExtrude","CAP_EDGE",EDGE,{"disambiguationData":[OSD([subQ1])],"isStart":true});var subQ3=makeQuery(id+"F1.opExtrude","CAP_VERTEX",VERTEX,{"disambiguationData":[OSD([subQ1,subQ0])],"isStart":true});Q23=makeQuery(id+"F11.boolean.opBoolean","SPLIT",EDGE,{"disambiguationData":[TD([makeQuery(id+"F11.opExtrude","SWEPT_FACE",FACE,{"disambiguationData":[OSD([sQuery(id+"F10.wireOp",EDGE,"E23.top")])]})])],"derivedFrom":makeQuery(id+"F2.opChamfer","BLEND_EDGE",EDGE,{"blendedFrom":[subQ3,subQ2],"blendedInto":[]})});}
            var Q24;
            {var subQ0=sQuery(id+"F0.wireOp",EDGE,"E0.left");var subQ1=sQuery(id+"F0.wireOp",EDGE,"E0.top");var subQ2=makeQuery(id+"F1.opExtrude","CAP_EDGE",EDGE,{"disambiguationData":[OSD([subQ1])],"isStart":true});var subQ3=makeQuery(id+"F1.opExtrude","CAP_VERTEX",VERTEX,{"disambiguationData":[OSD([subQ1,subQ0])],"isStart":true});Q24=makeQuery(id+"F11.boolean.opBoolean","SPLIT",EDGE,{"disambiguationData":[TD([makeQuery(id+"F11.opExtrude","SWEPT_FACE",FACE,{"disambiguationData":[OSD([sQuery(id+"F10.wireOp",EDGE,"E23.top")])]})])],"derivedFrom":makeQuery(id+"F2.opChamfer","BLEND_EDGE",EDGE,{"blendedFrom":[subQ3,subQ2],"blendedInto":[]})});}
            var Q25;
            {var subQ0=sQuery(id+"F0.wireOp",EDGE,"E0.right");Q25=makeQuery(id+"F2.opChamfer","BLEND_EDGE",EDGE,{"blendedFrom":[makeQuery(id+"F1.opExtrude","CAP_VERTEX",VERTEX,{"disambiguationData":[OSD([sQuery(id+"F0.wireOp",EDGE,"E0.top"),subQ0])],"isStart":true}),makeQuery(id+"F1.opExtrude","CAP_EDGE",EDGE,{"disambiguationData":[OSD([subQ0])],"isStart":true})],"blendedInto":[]});}
            var Q26;
            {var subQ0=sQuery(id+"F0.wireOp",EDGE,"E0.left");Q26=makeQuery(id+"F2.opChamfer","BLEND_EDGE",EDGE,{"blendedFrom":[makeQuery(id+"F1.opExtrude","CAP_VERTEX",VERTEX,{"disambiguationData":[OSD([sQuery(id+"F0.wireOp",EDGE,"E0.top"),subQ0])],"isStart":true}),makeQuery(id+"F1.opExtrude","CAP_EDGE",EDGE,{"disambiguationData":[OSD([subQ0])],"isStart":true})],"blendedInto":[]});}
            var Q27;
            {var subQ0=sQuery(id+"F0.wireOp",EDGE,"E0.left");var subQ1=sQuery(id+"F0.wireOp",EDGE,"E0.top");var subQ2=makeQuery(id+"F1.opExtrude","SWEPT_EDGE",EDGE,{"disambiguationData":[OSD([subQ1,subQ0])]});var subQ3=makeQuery(id+"F1.opExtrude","CAP_VERTEX",VERTEX,{"disambiguationData":[OSD([subQ1,subQ0])],"isStart":true});Q27=makeQuery(id+"F11.boolean.opBoolean","SPLIT",EDGE,{"disambiguationData":[TD([makeQuery(id+"F1.opExtrude","SWEPT_FACE",FACE,{"disambiguationData":[OSD([subQ0])]})])],"derivedFrom":makeQuery(id+"F2.opChamfer","BLEND_EDGE",EDGE,{"blendedFrom":[subQ3,subQ2],"blendedInto":[]})});}
            var Q28;
            {var subQ0=sQuery(id+"F0.wireOp",EDGE,"E0.right");Q28=makeQuery(id+"F2.opChamfer","BLEND_EDGE",EDGE,{"blendedFrom":[makeQuery(id+"F1.opExtrude","CAP_VERTEX",VERTEX,{"disambiguationData":[OSD([sQuery(id+"F0.wireOp",EDGE,"E0.top"),subQ0])],"isStart":false}),makeQuery(id+"F1.opExtrude","CAP_EDGE",EDGE,{"disambiguationData":[OSD([subQ0])],"isStart":false})],"blendedInto":[]});}
            var Q29;
            {var subQ0=sQuery(id+"F0.wireOp",EDGE,"E0.right");var subQ1=sQuery(id+"F0.wireOp",EDGE,"E0.top");var subQ2=makeQuery(id+"F1.opExtrude","CAP_EDGE",EDGE,{"disambiguationData":[OSD([subQ1])],"isStart":false});var subQ3=makeQuery(id+"F1.opExtrude","CAP_VERTEX",VERTEX,{"disambiguationData":[OSD([subQ1,subQ0])],"isStart":false});Q29=makeQuery(id+"F11.boolean.opBoolean","SPLIT",EDGE,{"disambiguationData":[TD([makeQuery(id+"F11.opExtrude","SWEPT_FACE",FACE,{"disambiguationData":[OSD([sQuery(id+"F10.wireOp",EDGE,"E23.bottom")])]})])],"derivedFrom":makeQuery(id+"F2.opChamfer","BLEND_EDGE",EDGE,{"blendedFrom":[subQ3,subQ2],"blendedInto":[]})});}
            fillet(context, id + "F28", {"entities" : qUnion([Q0, Q1, Q2, Q3, Q4, Q5, Q6, Q7, Q8, Q9, Q10, Q11, Q12, Q13, Q14, Q15, Q16, Q17, Q18, Q19, Q20, Q21, Q22, Q23, Q24, Q25, Q26, Q27, Q28, Q29]), "radius" : 2.54 * mm, "tangentPropagation" : true, "allowEdgeOverflow" : false});
        }
        {
            var Q0;
            {var subQ0=sQuery(id+"F0.wireOp",EDGE,"E0.bottom");Q0=makeQuery(id+"F2.opChamfer","BLEND_FACE",FACE,{"disambiguationData":[OSD([subQ0]),TDD([makeQuery(id+"F1.opExtrude","CAP_EDGE",EDGE,{"disambiguationData":[OSD([subQ0])],"isStart":false})])]});}
            var sketch = newSketch(context, id + "F29", { "sketchPlane" : qUnion([Q0])});
            skLineSegment(sketch, "E38.bottom", {"start": v(-1.27, 0) * mm, "end": v(1.27, 0) * mm});
            skLineSegment(sketch, "E38.top", {"start": v(-1.27, -17.96) * mm, "end": v(1.27, -17.96) * mm});
            skLineSegment(sketch, "E38.left", {"start": v(-1.27, 0) * mm, "end": v(-1.27, -17.96) * mm});
            skLineSegment(sketch, "E38.right", {"start": v(1.27, 0) * mm, "end": v(1.27, -17.96) * mm});
            skLineSegment(sketch, "E39.1.0.0", {"start": v(3.81, 0) * mm, "end": v(3.81, -17.96) * mm});
            skLineSegment(sketch, "E39.1.0.1", {"start": v(3.81, 0) * mm, "end": v(6.35, 0) * mm});
            skLineSegment(sketch, "E39.1.0.2", {"start": v(6.35, 0) * mm, "end": v(6.35, -17.96) * mm});
            skLineSegment(sketch, "E39.1.0.3", {"start": v(3.81, -17.96) * mm, "end": v(6.35, -17.96) * mm});
            skLineSegment(sketch, "E39.2.0.0", {"start": v(8.9, 0) * mm, "end": v(8.9, -17.96) * mm});
            skLineSegment(sketch, "E39.2.0.1", {"start": v(8.9, 0) * mm, "end": v(11.43, 0) * mm});
            skLineSegment(sketch, "E39.2.0.2", {"start": v(11.43, 0) * mm, "end": v(11.43, -17.96) * mm});
            skLineSegment(sketch, "E39.2.0.3", {"start": v(8.9, -17.96) * mm, "end": v(11.43, -17.96) * mm});
            skLineSegment(sketch, "E39.3.0.0", {"start": v(13.97, 0) * mm, "end": v(13.97, -17.96) * mm});
            skLineSegment(sketch, "E39.3.0.1", {"start": v(13.97, 0) * mm, "end": v(16.51, 0) * mm});
            skLineSegment(sketch, "E39.3.0.2", {"start": v(16.51, 0) * mm, "end": v(16.51, -17.96) * mm});
            skLineSegment(sketch, "E39.3.0.3", {"start": v(13.97, -17.96) * mm, "end": v(16.51, -17.96) * mm});
            skLineSegment(sketch, "E39.4.0.0", {"start": v(19.05, 0) * mm, "end": v(19.05, -17.96) * mm});
            skLineSegment(sketch, "E39.4.0.1", {"start": v(19.05, 0) * mm, "end": v(21.6, 0) * mm});
            skLineSegment(sketch, "E39.4.0.2", {"start": v(21.6, 0) * mm, "end": v(21.6, -17.96) * mm});
            skLineSegment(sketch, "E39.4.0.3", {"start": v(19.05, -17.96) * mm, "end": v(21.6, -17.96) * mm});
            skLineSegment(sketch, "E39.5.0.0", {"start": v(24.13, 0) * mm, "end": v(24.13, -17.96) * mm});
            skLineSegment(sketch, "E39.5.0.1", {"start": v(24.13, 0) * mm, "end": v(26.67, 0) * mm});
            skLineSegment(sketch, "E39.5.0.2", {"start": v(26.67, 0) * mm, "end": v(26.67, -17.96) * mm});
            skLineSegment(sketch, "E39.5.0.3", {"start": v(24.13, -17.96) * mm, "end": v(26.67, -17.96) * mm});
            skLineSegment(sketch, "E39.6.0.0", {"start": v(29.21, 0) * mm, "end": v(29.21, -17.96) * mm});
            skLineSegment(sketch, "E39.6.0.1", {"start": v(29.21, 0) * mm, "end": v(31.75, 0) * mm});
            skLineSegment(sketch, "E39.6.0.2", {"start": v(31.75, 0) * mm, "end": v(31.75, -17.96) * mm});
            skLineSegment(sketch, "E39.6.0.3", {"start": v(29.21, -17.96) * mm, "end": v(31.75, -17.96) * mm});
            skLineSegment(sketch, "E40.1.0.0", {"start": v(-6.35, -17.96) * mm, "end": v(-3.8, -17.96) * mm});
            skLineSegment(sketch, "E40.1.0.1", {"start": v(-6.35, 0) * mm, "end": v(-3.8, 0) * mm});
            skLineSegment(sketch, "E40.1.0.2", {"start": v(-6.35, 0) * mm, "end": v(-6.35, -17.96) * mm});
            skLineSegment(sketch, "E40.1.0.3", {"start": v(-3.8, 0) * mm, "end": v(-3.8, -17.96) * mm});
            skLineSegment(sketch, "E40.2.0.0", {"start": v(-11.43, -17.96) * mm, "end": v(-8.9, -17.96) * mm});
            skLineSegment(sketch, "E40.2.0.1", {"start": v(-11.43, 0) * mm, "end": v(-8.9, 0) * mm});
            skLineSegment(sketch, "E40.2.0.2", {"start": v(-11.43, 0) * mm, "end": v(-11.43, -17.96) * mm});
            skLineSegment(sketch, "E40.2.0.3", {"start": v(-8.9, 0) * mm, "end": v(-8.9, -17.96) * mm});
            skLineSegment(sketch, "E40.3.0.0", {"start": v(-16.51, -17.96) * mm, "end": v(-13.97, -17.96) * mm});
            skLineSegment(sketch, "E40.3.0.1", {"start": v(-16.51, 0) * mm, "end": v(-13.97, 0) * mm});
            skLineSegment(sketch, "E40.3.0.2", {"start": v(-16.51, 0) * mm, "end": v(-16.51, -17.96) * mm});
            skLineSegment(sketch, "E40.3.0.3", {"start": v(-13.97, 0) * mm, "end": v(-13.97, -17.96) * mm});
            skLineSegment(sketch, "E40.4.0.0", {"start": v(-21.6, -17.96) * mm, "end": v(-19.05, -17.96) * mm});
            skLineSegment(sketch, "E40.4.0.1", {"start": v(-21.6, 0) * mm, "end": v(-19.05, 0) * mm});
            skLineSegment(sketch, "E40.4.0.2", {"start": v(-21.6, 0) * mm, "end": v(-21.6, -17.96) * mm});
            skLineSegment(sketch, "E40.4.0.3", {"start": v(-19.05, 0) * mm, "end": v(-19.05, -17.96) * mm});
            skLineSegment(sketch, "E40.5.0.0", {"start": v(-26.67, -17.96) * mm, "end": v(-24.13, -17.96) * mm});
            skLineSegment(sketch, "E40.5.0.1", {"start": v(-26.67, 0) * mm, "end": v(-24.13, 0) * mm});
            skLineSegment(sketch, "E40.5.0.2", {"start": v(-26.67, 0) * mm, "end": v(-26.67, -17.96) * mm});
            skLineSegment(sketch, "E40.5.0.3", {"start": v(-24.13, 0) * mm, "end": v(-24.13, -17.96) * mm});
            skLineSegment(sketch, "E40.6.0.0", {"start": v(-31.75, -17.96) * mm, "end": v(-29.21, -17.96) * mm});
            skLineSegment(sketch, "E40.6.0.1", {"start": v(-31.75, 0) * mm, "end": v(-29.21, 0) * mm});
            skLineSegment(sketch, "E40.6.0.2", {"start": v(-31.75, 0) * mm, "end": v(-31.75, -17.96) * mm});
            skLineSegment(sketch, "E40.6.0.3", {"start": v(-29.21, 0) * mm, "end": v(-29.21, -17.96) * mm});
            skLineSegment(sketch, "E40.direction1", {"start": v(-1.27, -17.96) * mm, "end": v(-6.35, -17.96) * mm, "construction": true});
            skSolve(sketch);
        }
        {
            var Q0;
            Q0 = qSketchRegion(id + "F29", true);
            extrude(context, id + "F30", {"entities" : qUnion([Q0]), "operationType" : NewBodyOperationType.REMOVE, "oppositeDirection" : true, "depth" : 2.54 * mm, "offsetDistance" : 25.4 * mm});
        }
        {
            var Q0;
            Q0=makeQuery(id+"F30.boolean.opBoolean","COPY",EDGE,{"derivedFrom":makeQuery(id+"F30.opExtrude","CAP_EDGE",EDGE,{"disambiguationData":[OSD([sQuery(id+"F29.wireOp",EDGE,"E40.6.0.2")])],"isStart":false})});
            var Q1;
            Q1=makeQuery(id+"F30.boolean.opBoolean","COPY",EDGE,{"derivedFrom":makeQuery(id+"F30.opExtrude","CAP_EDGE",EDGE,{"disambiguationData":[OSD([sQuery(id+"F29.wireOp",EDGE,"E40.6.0.3")])],"isStart":false})});
            var Q2;
            Q2=makeQuery(id+"F30.boolean.opBoolean","COPY",EDGE,{"derivedFrom":makeQuery(id+"F30.opExtrude","CAP_EDGE",EDGE,{"disambiguationData":[OSD([sQuery(id+"F29.wireOp",EDGE,"E40.5.0.3")])],"isStart":false})});
            var Q3;
            Q3=makeQuery(id+"F30.boolean.opBoolean","COPY",EDGE,{"derivedFrom":makeQuery(id+"F30.opExtrude","CAP_EDGE",EDGE,{"disambiguationData":[OSD([sQuery(id+"F29.wireOp",EDGE,"E40.5.0.2")])],"isStart":false})});
            var Q4;
            Q4=makeQuery(id+"F30.boolean.opBoolean","COPY",EDGE,{"derivedFrom":makeQuery(id+"F30.opExtrude","CAP_EDGE",EDGE,{"disambiguationData":[OSD([sQuery(id+"F29.wireOp",EDGE,"E40.4.0.2")])],"isStart":false})});
            var Q5;
            Q5=makeQuery(id+"F30.boolean.opBoolean","COPY",EDGE,{"derivedFrom":makeQuery(id+"F30.opExtrude","CAP_EDGE",EDGE,{"disambiguationData":[OSD([sQuery(id+"F29.wireOp",EDGE,"E40.4.0.3")])],"isStart":false})});
            var Q6;
            Q6=makeQuery(id+"F30.boolean.opBoolean","COPY",EDGE,{"derivedFrom":makeQuery(id+"F30.opExtrude","CAP_EDGE",EDGE,{"disambiguationData":[OSD([sQuery(id+"F29.wireOp",EDGE,"E40.3.0.2")])],"isStart":false})});
            var Q7;
            Q7=makeQuery(id+"F30.boolean.opBoolean","COPY",EDGE,{"derivedFrom":makeQuery(id+"F30.opExtrude","CAP_EDGE",EDGE,{"disambiguationData":[OSD([sQuery(id+"F29.wireOp",EDGE,"E40.3.0.3")])],"isStart":false})});
            var Q8;
            Q8=makeQuery(id+"F30.boolean.opBoolean","COPY",EDGE,{"derivedFrom":makeQuery(id+"F30.opExtrude","CAP_EDGE",EDGE,{"disambiguationData":[OSD([sQuery(id+"F29.wireOp",EDGE,"E40.2.0.2")])],"isStart":false})});
            var Q9;
            Q9=makeQuery(id+"F30.boolean.opBoolean","COPY",EDGE,{"derivedFrom":makeQuery(id+"F30.opExtrude","CAP_EDGE",EDGE,{"disambiguationData":[OSD([sQuery(id+"F29.wireOp",EDGE,"E40.2.0.3")])],"isStart":false})});
            var Q10;
            Q10=makeQuery(id+"F30.boolean.opBoolean","COPY",EDGE,{"derivedFrom":makeQuery(id+"F30.opExtrude","CAP_EDGE",EDGE,{"disambiguationData":[OSD([sQuery(id+"F29.wireOp",EDGE,"E40.1.0.3")])],"isStart":false})});
            var Q11;
            Q11=makeQuery(id+"F30.boolean.opBoolean","COPY",EDGE,{"derivedFrom":makeQuery(id+"F30.opExtrude","CAP_EDGE",EDGE,{"disambiguationData":[OSD([sQuery(id+"F29.wireOp",EDGE,"E40.1.0.2")])],"isStart":false})});
            var Q12;
            Q12=makeQuery(id+"F30.boolean.opBoolean","COPY",EDGE,{"derivedFrom":makeQuery(id+"F30.opExtrude","CAP_EDGE",EDGE,{"disambiguationData":[OSD([sQuery(id+"F29.wireOp",EDGE,"E38.left")])],"isStart":false})});
            var Q13;
            Q13=makeQuery(id+"F30.boolean.opBoolean","COPY",EDGE,{"derivedFrom":makeQuery(id+"F30.opExtrude","CAP_EDGE",EDGE,{"disambiguationData":[OSD([sQuery(id+"F29.wireOp",EDGE,"E39.1.0.0")])],"isStart":false})});
            var Q14;
            Q14=makeQuery(id+"F30.boolean.opBoolean","COPY",EDGE,{"derivedFrom":makeQuery(id+"F30.opExtrude","CAP_EDGE",EDGE,{"disambiguationData":[OSD([sQuery(id+"F29.wireOp",EDGE,"E39.2.0.0")])],"isStart":false})});
            var Q15;
            Q15=makeQuery(id+"F30.boolean.opBoolean","COPY",EDGE,{"derivedFrom":makeQuery(id+"F30.opExtrude","CAP_EDGE",EDGE,{"disambiguationData":[OSD([sQuery(id+"F29.wireOp",EDGE,"E39.3.0.0")])],"isStart":false})});
            var Q16;
            Q16=makeQuery(id+"F30.boolean.opBoolean","COPY",EDGE,{"derivedFrom":makeQuery(id+"F30.opExtrude","CAP_EDGE",EDGE,{"disambiguationData":[OSD([sQuery(id+"F29.wireOp",EDGE,"E39.4.0.0")])],"isStart":false})});
            var Q17;
            Q17=makeQuery(id+"F30.boolean.opBoolean","COPY",EDGE,{"derivedFrom":makeQuery(id+"F30.opExtrude","CAP_EDGE",EDGE,{"disambiguationData":[OSD([sQuery(id+"F29.wireOp",EDGE,"E39.5.0.0")])],"isStart":false})});
            var Q18;
            Q18=makeQuery(id+"F30.boolean.opBoolean","COPY",EDGE,{"derivedFrom":makeQuery(id+"F30.opExtrude","CAP_EDGE",EDGE,{"disambiguationData":[OSD([sQuery(id+"F29.wireOp",EDGE,"E39.6.0.0")])],"isStart":false})});
            var Q19;
            Q19=makeQuery(id+"F30.boolean.opBoolean","COPY",EDGE,{"derivedFrom":makeQuery(id+"F30.opExtrude","CAP_EDGE",EDGE,{"disambiguationData":[OSD([sQuery(id+"F29.wireOp",EDGE,"E39.6.0.2")])],"isStart":false})});
            var Q20;
            Q20=makeQuery(id+"F30.boolean.opBoolean","COPY",EDGE,{"derivedFrom":makeQuery(id+"F30.opExtrude","CAP_EDGE",EDGE,{"disambiguationData":[OSD([sQuery(id+"F29.wireOp",EDGE,"E39.5.0.2")])],"isStart":false})});
            var Q21;
            Q21=makeQuery(id+"F30.boolean.opBoolean","COPY",EDGE,{"derivedFrom":makeQuery(id+"F30.opExtrude","CAP_EDGE",EDGE,{"disambiguationData":[OSD([sQuery(id+"F29.wireOp",EDGE,"E39.4.0.2")])],"isStart":false})});
            var Q22;
            Q22=makeQuery(id+"F30.boolean.opBoolean","COPY",EDGE,{"derivedFrom":makeQuery(id+"F30.opExtrude","CAP_EDGE",EDGE,{"disambiguationData":[OSD([sQuery(id+"F29.wireOp",EDGE,"E39.3.0.2")])],"isStart":false})});
            var Q23;
            Q23=makeQuery(id+"F30.boolean.opBoolean","COPY",EDGE,{"derivedFrom":makeQuery(id+"F30.opExtrude","CAP_EDGE",EDGE,{"disambiguationData":[OSD([sQuery(id+"F29.wireOp",EDGE,"E39.2.0.2")])],"isStart":false})});
            var Q24;
            Q24=makeQuery(id+"F30.boolean.opBoolean","COPY",EDGE,{"derivedFrom":makeQuery(id+"F30.opExtrude","CAP_EDGE",EDGE,{"disambiguationData":[OSD([sQuery(id+"F29.wireOp",EDGE,"E39.1.0.2")])],"isStart":false})});
            var Q25;
            Q25=makeQuery(id+"F30.boolean.opBoolean","COPY",EDGE,{"derivedFrom":makeQuery(id+"F30.opExtrude","CAP_EDGE",EDGE,{"disambiguationData":[OSD([sQuery(id+"F29.wireOp",EDGE,"E38.right")])],"isStart":false})});
            fillet(context, id + "F31", {"entities" : qUnion([Q0, Q1, Q2, Q3, Q4, Q5, Q6, Q7, Q8, Q9, Q10, Q11, Q12, Q13, Q14, Q15, Q16, Q17, Q18, Q19, Q20, Q21, Q22, Q23, Q24, Q25]), "radius" : 1.27 * mm, "tangentPropagation" : true, "allowEdgeOverflow" : false});
        }
    });
